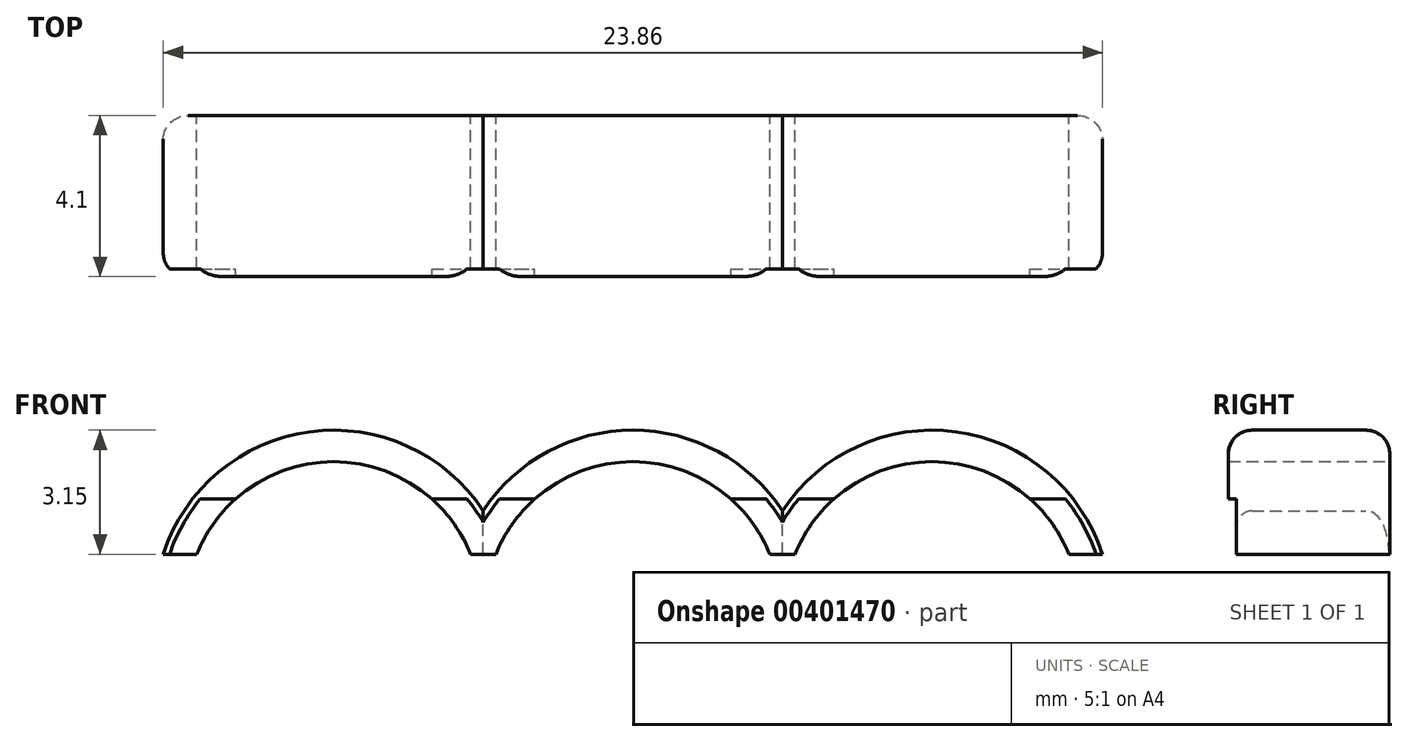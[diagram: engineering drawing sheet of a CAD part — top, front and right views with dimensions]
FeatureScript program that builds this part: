
annotation { "Feature Type Name" : "Feature", "Feature Type Description" : "" }
export const myFeature = defineFeature(function(context is Context, id is Id, definition is map)
    precondition{}
    {
        {
            var Q0;
            Q0=qCreatedBy(makeId("Front.planeOp"),FACE);
            var sketch = newSketch(context, id + "F0", { "sketchPlane" : qUnion([Q0])});
            skLineSegment(sketch, "E0", {"start": v(0, 0) * mm, "end": v(7.6, 0) * mm, "construction": true});
            skLineSegment(sketch, "E1", {"start": v(7.6, 0) * mm, "end": v(15.2, 0) * mm, "construction": true});
            skLineSegment(sketch, "E2", {"start": v(-4.33, 1.4) * mm, "end": v(-3.48, 1.4) * mm});
            skLineSegment(sketch, "E3.trimOffspring", {"start": v(3.48, 1.4) * mm, "end": v(4.12, 1.4) * mm});
            skLineSegment(sketch, "E4.trimOffspring", {"start": v(11.08, 1.4) * mm, "end": v(11.72, 1.4) * mm});
            skArc(sketch, "E5.trimOffspring", {"start": v(3.8, 2.5) * mm, "mid": v(-0.61, 4.5) * mm, "end": v(-4.33, 1.4) * mm});
            skArc(sketch, "E6.trimOffspring", {"start": v(3.48, 1.4) * mm, "mid": v(0, 3.75) * mm, "end": v(-3.48, 1.4) * mm});
            skArc(sketch, "E7.trimOffspring", {"start": v(11.4, 2.5) * mm, "mid": v(7.6, 4.55) * mm, "end": v(3.8, 2.5) * mm});
            skArc(sketch, "E8.trimOffspring", {"start": v(11.08, 1.4) * mm, "mid": v(7.6, 3.75) * mm, "end": v(4.12, 1.4) * mm});
            skLineSegment(sketch, "E9.trimOffspring", {"start": v(18.68, 1.4) * mm, "end": v(19.53, 1.4) * mm});
            skArc(sketch, "E10.trimOffspring", {"start": v(19.53, 1.4) * mm, "mid": v(15.81, 4.5) * mm, "end": v(11.4, 2.5) * mm});
            skArc(sketch, "E11.trimOffspring", {"start": v(18.68, 1.4) * mm, "mid": v(15.2, 3.75) * mm, "end": v(11.72, 1.4) * mm});
            skSolve(sketch);
        }
        {
            var Q0;
            Q0 = qSketchRegion(id + "F0", true);
            extrude(context, id + "F1", {"entities" : qUnion([Q0]), "depth" : 4.1 * mm});
        }
        {
            var Q0;
            Q0=makeQuery(id+"F1.opExtrude","CAP_EDGE",EDGE,{"disambiguationData":[OSD([sQuery(id+"F0.wireOp",EDGE,"E5.trimOffspring")])],"isStart":false});
            var Q1;
            Q1=makeQuery(id+"F1.opExtrude","CAP_EDGE",EDGE,{"disambiguationData":[OSD([sQuery(id+"F0.wireOp",EDGE,"E7.trimOffspring")])],"isStart":false});
            var Q2;
            Q2=makeQuery(id+"F1.opExtrude","CAP_EDGE",EDGE,{"disambiguationData":[OSD([sQuery(id+"F0.wireOp",EDGE,"E10.trimOffspring")])],"isStart":false});
            var Q3;
            Q3=makeQuery(id+"F1.opExtrude","CAP_EDGE",EDGE,{"disambiguationData":[OSD([sQuery(id+"F0.wireOp",EDGE,"E5.trimOffspring")])],"isStart":true});
            var Q4;
            Q4=makeQuery(id+"F1.opExtrude","CAP_EDGE",EDGE,{"disambiguationData":[OSD([sQuery(id+"F0.wireOp",EDGE,"E7.trimOffspring")])],"isStart":true});
            var Q5;
            Q5=makeQuery(id+"F1.opExtrude","CAP_EDGE",EDGE,{"disambiguationData":[OSD([sQuery(id+"F0.wireOp",EDGE,"E10.trimOffspring")])],"isStart":true});
            fillet(context, id + "F2", {"entities" : qUnion([Q0, Q1, Q2, Q3, Q4, Q5]), "radius" : 0.6 * mm, "tangentPropagation" : true, "allowEdgeOverflow" : false});
        }
        {
            var Q0;
            Q0=qCreatedBy(makeId("Right.planeOp"),FACE);
            var sketch = newSketch(context, id + "F3", { "sketchPlane" : qUnion([Q0])});
            skLineSegment(sketch, "E12.bottom", {"start": v(-4.1, 2.8) * mm, "end": v(-3.9, 2.8) * mm});
            skLineSegment(sketch, "E12.top", {"start": v(-4.1, 1.4) * mm, "end": v(-3.9, 1.4) * mm});
            skLineSegment(sketch, "E12.left", {"start": v(-4.1, 1.4) * mm, "end": v(-4.1, 2.8) * mm});
            skLineSegment(sketch, "E12.right", {"start": v(-3.9, 1.4) * mm, "end": v(-3.9, 2.8) * mm});
            skSolve(sketch);
        }
        {
            var Q0;
            Q0 = qSketchRegion(id + "F3", true);
            extrude(context, id + "F4", {"entities" : qUnion([Q0]), "operationType" : NewBodyOperationType.REMOVE, "endBound" : BoundingType.THROUGH_ALL, "oppositeDirection" : true, "depth" : 25 * mm, "hasSecondDirection" : true, "secondDirectionBound" : SecondDirectionBoundingType.THROUGH_ALL, "secondDirectionOppositeDirection" : false, "secondDirectionDepth" : 25 * mm});
        }
    });
